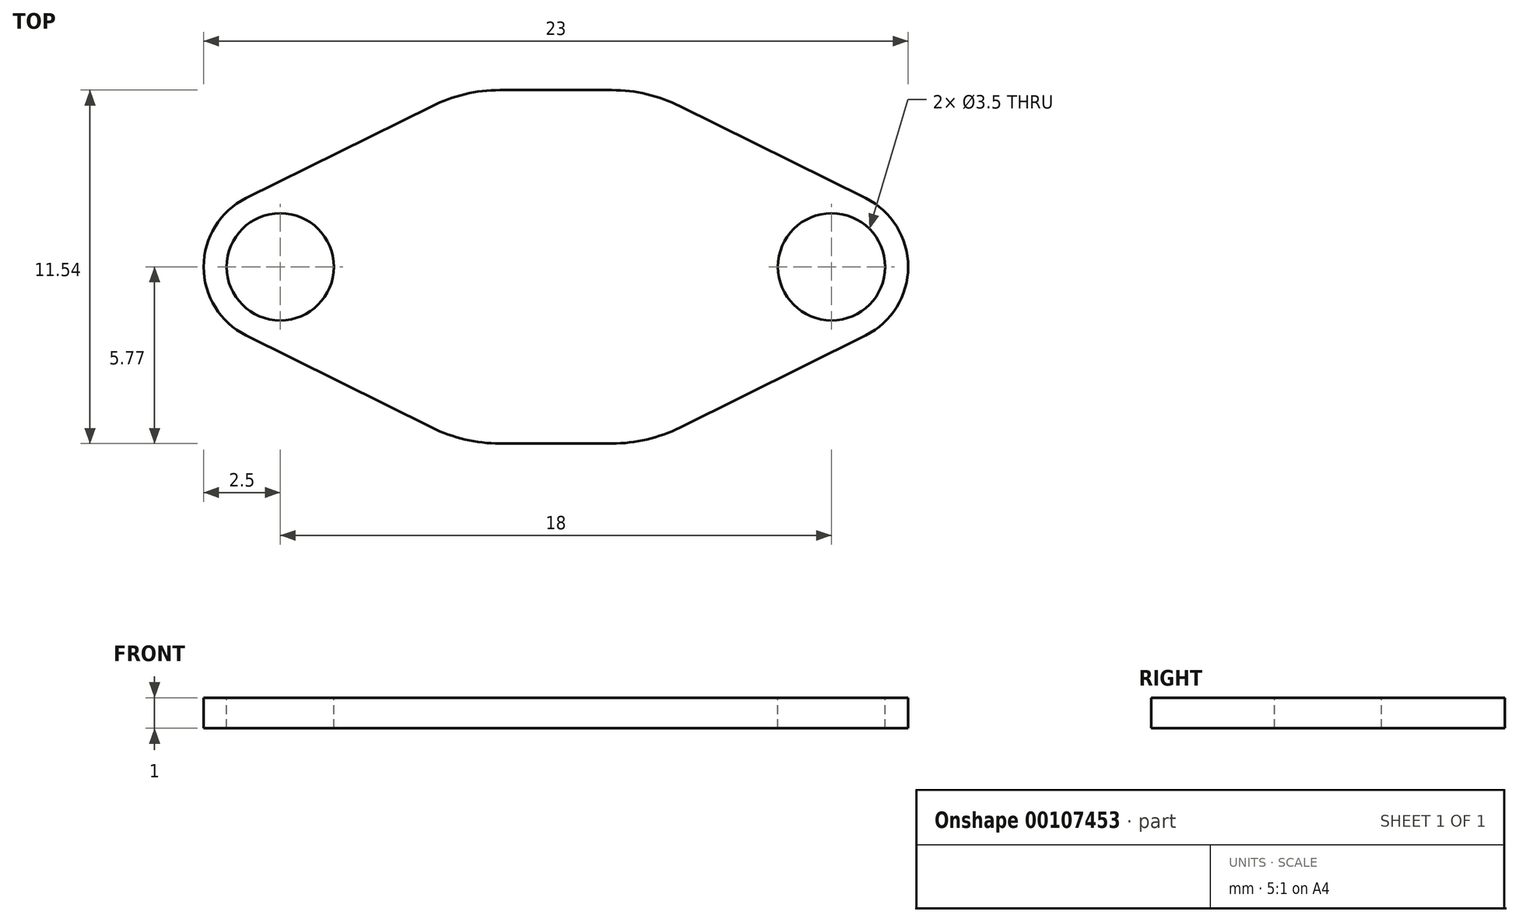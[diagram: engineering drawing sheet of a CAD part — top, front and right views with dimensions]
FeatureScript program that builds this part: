
annotation { "Feature Type Name" : "Feature", "Feature Type Description" : "" }
export const myFeature = defineFeature(function(context is Context, id is Id, definition is map)
    precondition{}
    {
        {
            assignVariable(context, id + "F0", {"name" : "e3d_height", "anyValue" : 62.3 - 16.7});
        }
        {
            assignVariable(context, id + "F1", {"name" : "bltouch_height", "anyValue" : 36.3});
        }
        {
            assignVariable(context, id + "F2", {"name" : "bltouch_offset", "anyValue" : 8.3});
        }
        {
            var Q0;
            Q0=qCreatedBy(makeId("Top.planeOp"),FACE);
            cPlane(context, id + "F3", {"entities" : qUnion([Q0]), "cplaneType" : CPlaneType.OFFSET, "offset" : (getVariable(context, 'e3d_height') - getVariable(context, 'bltouch_height') - getVariable(context, 'bltouch_offset')) * mm, "width" : 150 * mm, "height" : 150 * mm});
        }
        {
            var Q0;
            Q0=qCreatedBy(id+"F3.planeOp",FACE);
            var sketch = newSketch(context, id + "F4", { "sketchPlane" : qUnion([Q0])});
            skCircle(sketch, "E0", {"center": v(-9, 0) * mm, "radius": 1.75 * mm});
            skArc(sketch, "E1", {"start": v(-10.11, 2.24) * mm, "mid": v(-11.5, 0) * mm, "end": v(-10.11, -2.24) * mm});
            skLineSegment(sketch, "E2", {"start": v(-1.83, 5.77) * mm, "end": v(0, 5.77) * mm});
            skLineSegment(sketch, "E3", {"start": v(-4.05, 5.25) * mm, "end": v(-10.11, 2.24) * mm});
            skArc(sketch, "E4.MirrorCS", {"start": v(10.11, 2.24) * mm, "mid": v(11.5, 0) * mm, "end": v(10.11, -2.24) * mm});
            skCircle(sketch, "E5.MirrorC", {"center": v(9, 0) * mm, "radius": 1.75 * mm});
            skPoint(sketch, "E6.visualSharp", {"position": v(-3, 5.77) * mm});
            skArc(sketch, "E6.filletArc", {"start": v(-1.83, 5.77) * mm, "mid": v(-2.97, 5.64) * mm, "end": v(-4.05, 5.25) * mm});
            skArc(sketch, "E7.MirrorCS", {"start": v(-1.83, -5.77) * mm, "mid": v(-2.97, -5.64) * mm, "end": v(-4.05, -5.25) * mm});
            skArc(sketch, "E8.MirrorCS", {"start": v(1.83, 5.77) * mm, "mid": v(2.97, 5.64) * mm, "end": v(4.05, 5.25) * mm});
            skArc(sketch, "E9.MirrorCS", {"start": v(1.83, -5.77) * mm, "mid": v(2.97, -5.64) * mm, "end": v(4.05, -5.25) * mm});
            skLineSegment(sketch, "E10.MirrorCS", {"start": v(-1.83, -5.77) * mm, "end": v(0, -5.77) * mm});
            skLineSegment(sketch, "E11.MirrorCS", {"start": v(-4.05, -5.25) * mm, "end": v(-10.11, -2.24) * mm});
            skLineSegment(sketch, "E12.MirrorCS", {"start": v(1.83, 5.77) * mm, "end": v(0, 5.77) * mm});
            skLineSegment(sketch, "E13.MirrorCS", {"start": v(4.05, 5.25) * mm, "end": v(10.11, 2.24) * mm});
            skLineSegment(sketch, "E14.MirrorCS", {"start": v(4.05, -5.25) * mm, "end": v(10.11, -2.24) * mm});
            skLineSegment(sketch, "E15.MirrorCS", {"start": v(1.83, -5.77) * mm, "end": v(0, -5.77) * mm});
            skSolve(sketch);
        }
        {
            var Q0;
            Q0=makeQuery(id+"F4.imprint","IMPRINT",FACE,{"disambiguationData":[TD([[makeQuery(id+"F4.imprint","IMPRINT",EDGE,{"derivedFrom":sQuery(id+"F4.wireOp",EDGE,"E0")}),-1.0]])]});
            var Q1;
            Q1=qCreatedBy(makeId("Top.planeOp"),FACE);
            extrude(context, id + "F5", {"entities" : qUnion([Q0]), "endBound" : BoundingType.UP_TO_SURFACE, "oppositeDirection" : true, "endBoundEntityFace" : qUnion([Q1]), "depth" : 25 * mm});
        }
    });
